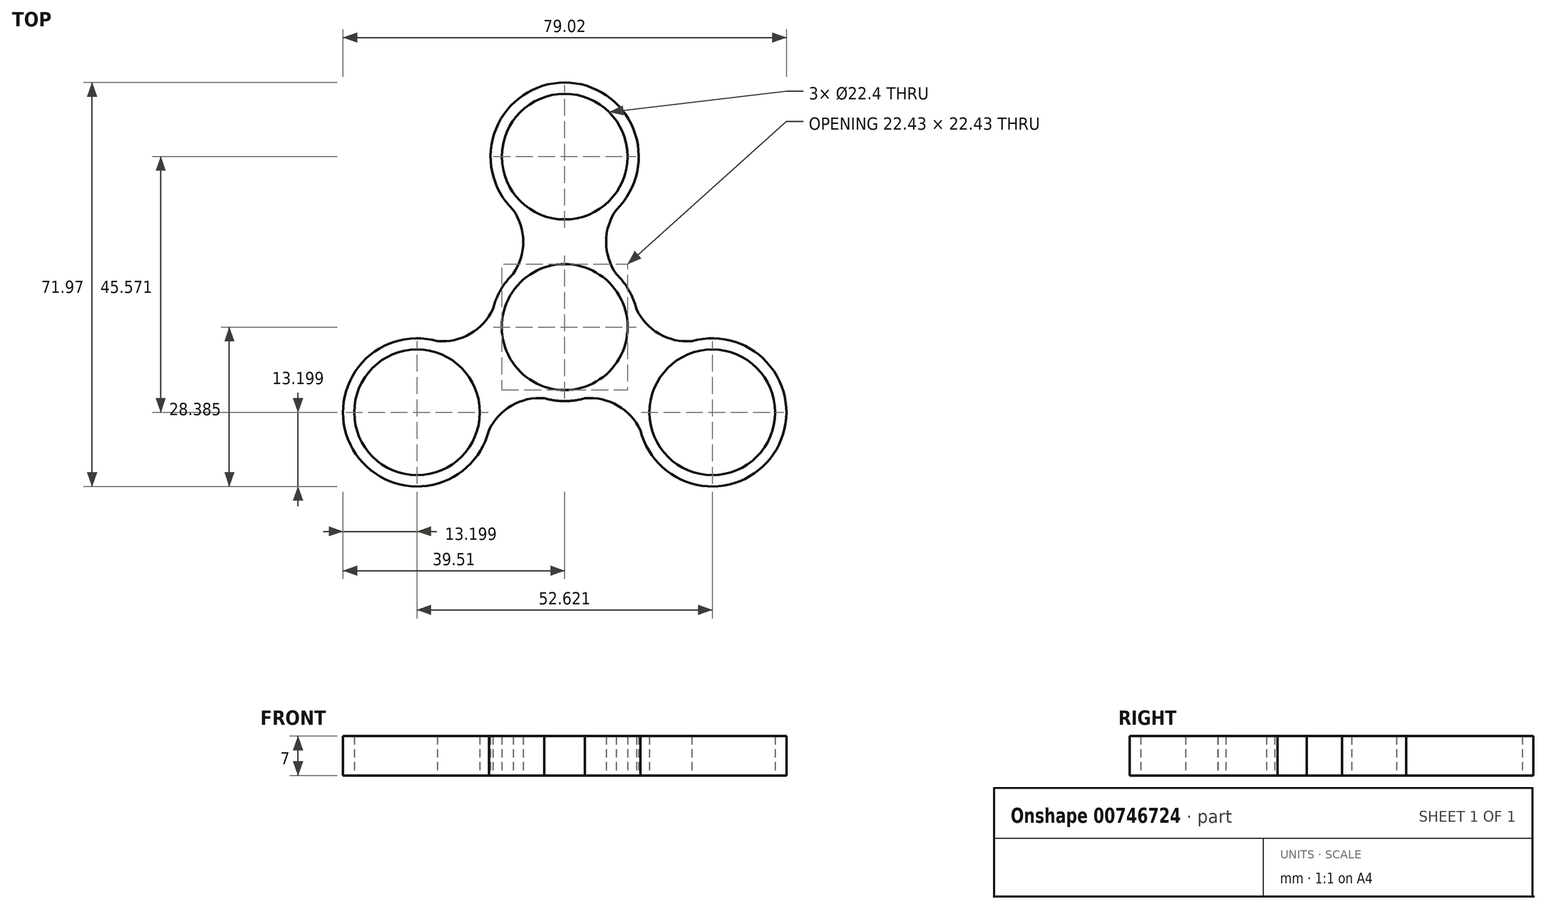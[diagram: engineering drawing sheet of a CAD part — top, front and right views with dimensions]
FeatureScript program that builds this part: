
annotation { "Feature Type Name" : "Feature", "Feature Type Description" : "" }
export const myFeature = defineFeature(function(context is Context, id is Id, definition is map)
    precondition{}
    {
        {
            var Q0;
            Q0=qCreatedBy(makeId("Top.planeOp"),FACE);
            var sketch = newSketch(context, id + "F0", { "sketchPlane" : qUnion([Q0])});
            skCircle(sketch, "E0", {"center": v(0, 0) * mm, "radius": 11.2 * mm});
            skArc(sketch, "E1", {"start": v(-9.17, 9.5) * mm, "mid": v(-11.43, 6.6) * mm, "end": v(-12.81, 3.18) * mm});
            skCircle(sketch, "E2", {"center": v(0, 30.4) * mm, "radius": 11.2 * mm});
            skArc(sketch, "E3", {"start": v(9.16, 20.9) * mm, "mid": v(0, 43.6) * mm, "end": v(-9.16, 20.9) * mm});
            skArc(sketch, "E4", {"start": v(-9.17, 9.5) * mm, "mid": v(-7.38, 15.2) * mm, "end": v(-9.16, 20.9) * mm});
            skArc(sketch, "E5", {"start": v(9.16, 20.9) * mm, "mid": v(7.38, 15.2) * mm, "end": v(9.17, 9.5) * mm});
            skCircle(sketch, "E6.1.0", {"center": v(-26.31, -15.17) * mm, "radius": 11.2 * mm});
            skArc(sketch, "E6.1.1", {"start": v(-22.66, -2.49) * mm, "mid": v(-37.74, -21.77) * mm, "end": v(-13.5, -18.35) * mm});
            skArc(sketch, "E6.1.2", {"start": v(-22.66, -2.49) * mm, "mid": v(-16.83, -1.18) * mm, "end": v(-12.8, 3.22) * mm});
            skArc(sketch, "E6.1.3", {"start": v(-3.62, -12.66) * mm, "mid": v(-9.45, -13.96) * mm, "end": v(-13.5, -18.35) * mm});
            skCircle(sketch, "E6.1.4", {"center": v(0.02, 0.03) * mm, "radius": 11.2 * mm});
            skArc(sketch, "E6.1.5", {"start": v(-3.62, -12.66) * mm, "mid": v(0.02, -13.17) * mm, "end": v(3.67, -12.66) * mm});
            skCircle(sketch, "E6.2.0", {"center": v(26.31, -15.17) * mm, "radius": 11.2 * mm});
            skArc(sketch, "E6.2.1", {"start": v(13.5, -18.35) * mm, "mid": v(37.74, -21.77) * mm, "end": v(22.66, -2.49) * mm});
            skArc(sketch, "E6.2.2", {"start": v(13.5, -18.35) * mm, "mid": v(9.45, -13.96) * mm, "end": v(3.62, -12.66) * mm});
            skArc(sketch, "E6.2.3", {"start": v(12.8, 3.22) * mm, "mid": v(16.83, -1.18) * mm, "end": v(22.66, -2.49) * mm});
            skCircle(sketch, "E6.2.4", {"center": v(-0.02, 0.03) * mm, "radius": 11.2 * mm});
            skArc(sketch, "E6.2.5", {"start": v(12.8, 3.22) * mm, "mid": v(11.41, 6.63) * mm, "end": v(9.14, 9.53) * mm});
            skPoint(sketch, "E6.center", {"position": v(0, 0.02) * mm});
            skArc(sketch, "E7.trimOffspring", {"start": v(-3.67, -12.66) * mm, "mid": v(-0.02, -13.17) * mm, "end": v(3.62, -12.66) * mm});
            skArc(sketch, "E8.trimOffspring", {"start": v(12.86, 3.08) * mm, "mid": v(11.45, 6.63) * mm, "end": v(9.08, 9.62) * mm});
            skArc(sketch, "E9.trimOffspring", {"start": v(-3.78, -12.65) * mm, "mid": v(0, -13.2) * mm, "end": v(3.78, -12.65) * mm});
            skArc(sketch, "E10.trimOffspring", {"start": v(12.81, 3.18) * mm, "mid": v(11.43, 6.6) * mm, "end": v(9.17, 9.5) * mm});
            skArc(sketch, "E11.trimOffspring", {"start": v(-9.08, 9.62) * mm, "mid": v(-11.45, 6.63) * mm, "end": v(-12.86, 3.08) * mm});
            skArc(sketch, "E12.trimOffspring", {"start": v(-9.14, 9.53) * mm, "mid": v(-11.41, 6.63) * mm, "end": v(-12.8, 3.22) * mm});
            skArc(sketch, "E13", {"start": v(-47.43, 0) * mm, "mid": v(-45.66, -12.25) * mm, "end": v(-37.74, -21.77) * mm});
            skLineSegment(sketch, "E14", {"start": v(-47.43, 0) * mm, "end": v(-37.09, -7.55) * mm});
            skSolve(sketch);
        }
        {
            var Q0;
            Q0=makeQuery(id+"F0.imprint","IMPRINT",FACE,{"disambiguationData":[TD([[makeQuery(id+"F0.imprint","IMPRINT",EDGE,{"derivedFrom":sQuery(id+"F0.wireOp",EDGE,"E2")}),-1.0]])]});
            extrude(context, id + "F1", {"entities" : qUnion([Q0]), "depth" : 7 * mm, "offsetDistance" : 25 * mm});
        }
    });
